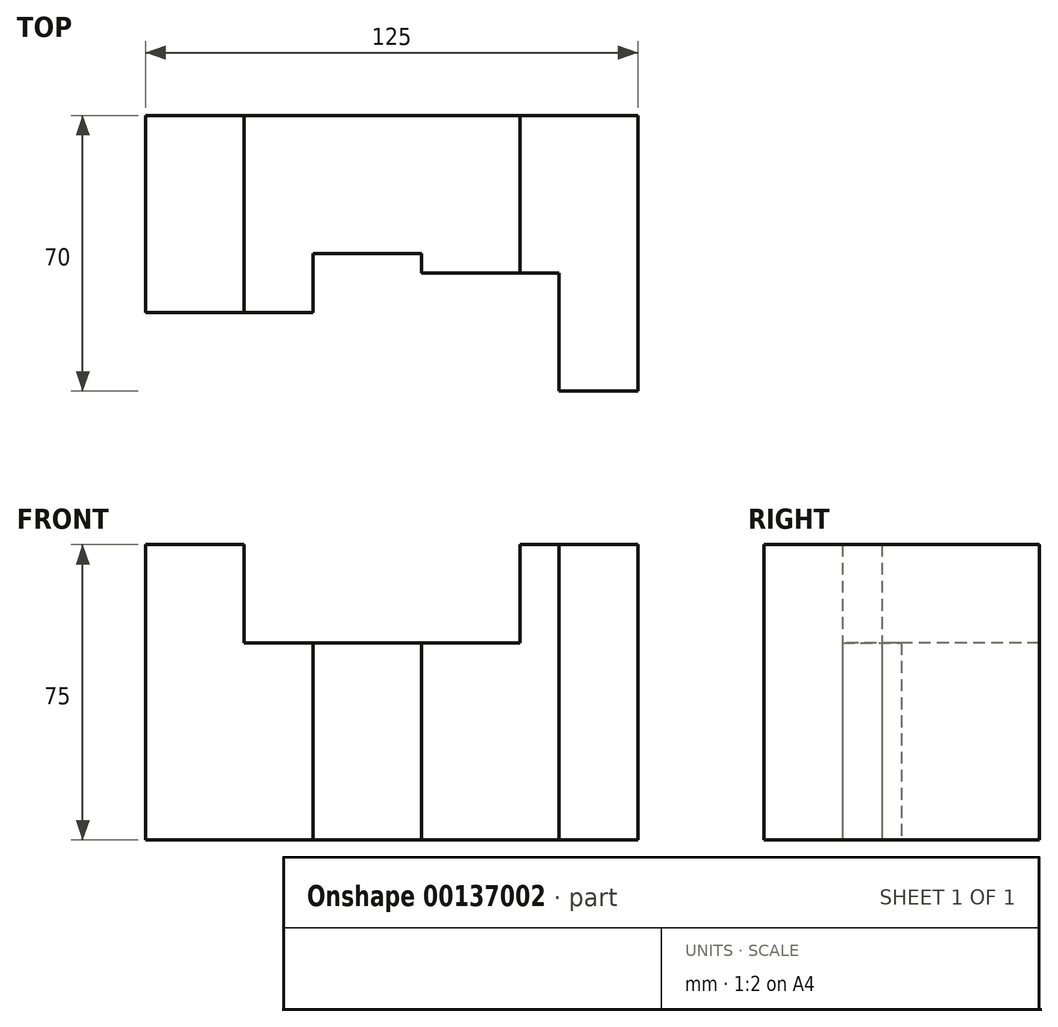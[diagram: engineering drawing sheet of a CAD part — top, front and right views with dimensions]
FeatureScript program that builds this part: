
annotation { "Feature Type Name" : "Feature", "Feature Type Description" : "" }
export const myFeature = defineFeature(function(context is Context, id is Id, definition is map)
    precondition{}
    {
        {
            var Q0;
            Q0=qCreatedBy(makeId("Top.planeOp"),FACE);
            var sketch = newSketch(context, id + "F0", { "sketchPlane" : qUnion([Q0])});
            skLineSegment(sketch, "E0", {"start": v(0, 0) * mm, "end": v(0, -50) * mm});
            skLineSegment(sketch, "E1", {"start": v(0, -50) * mm, "end": v(42.5, -50) * mm});
            skLineSegment(sketch, "E2", {"start": v(42.5, -50) * mm, "end": v(42.5, -35) * mm});
            skLineSegment(sketch, "E3", {"start": v(42.5, -35) * mm, "end": v(70, -35) * mm});
            skLineSegment(sketch, "E4", {"start": v(70, -35) * mm, "end": v(70, -40) * mm});
            skLineSegment(sketch, "E5", {"start": v(70, -40) * mm, "end": v(105, -40) * mm});
            skLineSegment(sketch, "E6", {"start": v(105, -40) * mm, "end": v(105, -70) * mm});
            skLineSegment(sketch, "E7", {"start": v(105, -70) * mm, "end": v(125, -70) * mm});
            skLineSegment(sketch, "E8", {"start": v(125, -70) * mm, "end": v(125, 0) * mm});
            skLineSegment(sketch, "E9", {"start": v(125, 0) * mm, "end": v(0, 0) * mm});
            skSolve(sketch);
        }
        {
            var Q0;
            Q0 = qSketchRegion(id + "F0", true);
            extrude(context, id + "F1", {"entities" : qUnion([Q0]), "depth" : 50 * mm});
        }
        {
            var Q0;
            Q0=makeQuery(id+"F1.opExtrude","CAP_FACE",FACE,{"disambiguationData":[OSD([sQuery(id+"F0.wireOp",EDGE,"E0"),sQuery(id+"F0.wireOp",EDGE,"E1"),sQuery(id+"F0.wireOp",EDGE,"E2"),sQuery(id+"F0.wireOp",EDGE,"E3"),sQuery(id+"F0.wireOp",EDGE,"E4"),sQuery(id+"F0.wireOp",EDGE,"E5"),sQuery(id+"F0.wireOp",EDGE,"E6"),sQuery(id+"F0.wireOp",EDGE,"E7"),sQuery(id+"F0.wireOp",EDGE,"E8"),sQuery(id+"F0.wireOp",EDGE,"E9")])],"isStart":false});
            var sketch = newSketch(context, id + "F2", { "sketchPlane" : qUnion([Q0])});
            skLineSegment(sketch, "E10.bottom", {"start": v(0, 0) * mm, "end": v(25, 0) * mm});
            skLineSegment(sketch, "E10.top", {"start": v(0, -50) * mm, "end": v(25, -50) * mm});
            skLineSegment(sketch, "E10.left", {"start": v(0, 0) * mm, "end": v(0, -50) * mm});
            skLineSegment(sketch, "E10.right", {"start": v(25, 0) * mm, "end": v(25, -50) * mm});
            skLineSegment(sketch, "E11.bottom", {"start": v(105, -70) * mm, "end": v(125, -70) * mm});
            skLineSegment(sketch, "E11.top", {"start": v(105, 0) * mm, "end": v(125, 0) * mm});
            skLineSegment(sketch, "E11.left", {"start": v(105, -70) * mm, "end": v(105, 0) * mm});
            skLineSegment(sketch, "E11.right", {"start": v(125, -70) * mm, "end": v(125, 0) * mm});
            skLineSegment(sketch, "E12.bottom", {"start": v(105, 0) * mm, "end": v(95, 0) * mm});
            skLineSegment(sketch, "E12.top", {"start": v(105, -40) * mm, "end": v(95, -40) * mm});
            skLineSegment(sketch, "E12.left", {"start": v(105, 0) * mm, "end": v(105, -40) * mm});
            skLineSegment(sketch, "E12.right", {"start": v(95, 0) * mm, "end": v(95, -40) * mm});
            skSolve(sketch);
        }
        {
            var Q0;
            Q0 = qSketchRegion(id + "F2", true);
            extrude(context, id + "F3", {"entities" : qUnion([Q0]), "operationType" : NewBodyOperationType.ADD, "depth" : 25 * mm});
        }
    });
